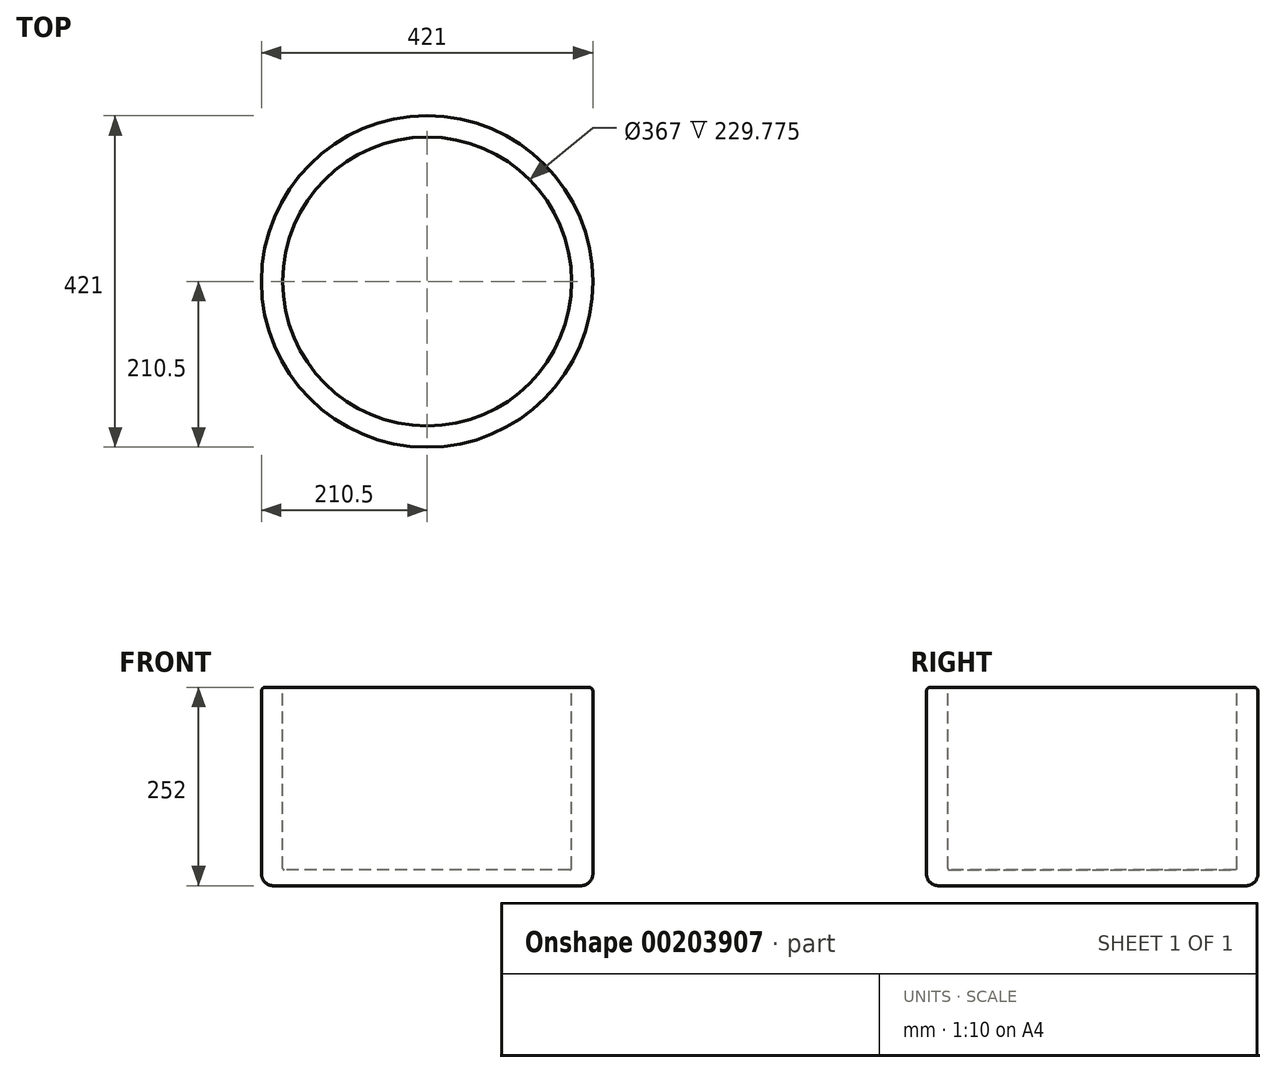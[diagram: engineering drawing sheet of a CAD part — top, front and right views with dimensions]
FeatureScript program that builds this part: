
annotation { "Feature Type Name" : "Feature", "Feature Type Description" : "" }
export const myFeature = defineFeature(function(context is Context, id is Id, definition is map)
    precondition{}
    {
        {
            var Q0;
            Q0=qCreatedBy(makeId("Top.planeOp"),FACE);
            var sketch = newSketch(context, id + "F0", { "sketchPlane" : qUnion([Q0])});
            skCircle(sketch, "E0", {"center": v(0, 0) * mm, "radius": 210.5 * mm});
            skSolve(sketch);
        }
        {
            var Q0;
            Q0=makeQuery(id+"F0.imprint","IMPRINT",FACE,{"disambiguationData":[TD([[makeQuery(id+"F0.imprint","IMPRINT",EDGE,{"derivedFrom":sQuery(id+"F0.wireOp",EDGE,"E0")}),1.0]])]});
            extrude(context, id + "F1", {"entities" : qUnion([Q0]), "depth" : 252 * mm, "offsetDistance" : 25 * mm});
        }
        {
            var Q0;
            Q0=makeQuery(id+"F1.opExtrude","CAP_FACE",FACE,{"disambiguationData":[OSD([sQuery(id+"F0.wireOp",EDGE,"E0")])],"isStart":false});
            var sketch = newSketch(context, id + "F2", { "sketchPlane" : qUnion([Q0])});
            skCircle(sketch, "E1", {"center": v(0, 0) * mm, "radius": 183.5 * mm});
            skSolve(sketch);
        }
        {
            var Q0;
            Q0=makeQuery(id+"F2.imprint","IMPRINT",FACE,{"disambiguationData":[TD([[makeQuery(id+"F2.imprint","IMPRINT",EDGE,{"derivedFrom":sQuery(id+"F2.wireOp",EDGE,"E1")}),1.0]])]});
            extrude(context, id + "F3", {"entities" : qUnion([Q0]), "operationType" : NewBodyOperationType.REMOVE, "oppositeDirection" : true, "depth" : 231.78 * mm});
        }
        {
            var Q0;
            Q0=makeQuery(id+"F1.opExtrude","CAP_EDGE",EDGE,{"disambiguationData":[OSD([sQuery(id+"F0.wireOp",EDGE,"E0")])],"isStart":true});
            fillet(context, id + "F4", {"entities" : qUnion([Q0]), "radius" : 15 * mm, "tangentPropagation" : true, "allowEdgeOverflow" : false});
        }
        {
            var Q0;
            Q0=makeQuery(id+"F1.opExtrude","CAP_EDGE",EDGE,{"disambiguationData":[OSD([sQuery(id+"F0.wireOp",EDGE,"E0")])],"isStart":false});
            fillet(context, id + "F5", {"entities" : qUnion([Q0]), "radius" : 5 * mm, "tangentPropagation" : true, "allowEdgeOverflow" : false});
        }
        {
            var Q0;
            Q0=makeQuery(id+"F3.boolean.opBoolean","COPY",EDGE,{"derivedFrom":makeQuery(id+"F3.opExtrude","CAP_EDGE",EDGE,{"disambiguationData":[OSD([sQuery(id+"F2.wireOp",EDGE,"E1")])],"isStart":true})});
            var Q1;
            Q1=makeQuery(id+"F3.boolean.opBoolean","COPY",EDGE,{"derivedFrom":makeQuery(id+"F3.opExtrude","CAP_EDGE",EDGE,{"disambiguationData":[OSD([sQuery(id+"F2.wireOp",EDGE,"E1")])],"isStart":false})});
            fillet(context, id + "F6", {"entities" : qUnion([Q0, Q1]), "radius" : 2 * mm, "tangentPropagation" : true, "allowEdgeOverflow" : false});
        }
    });
